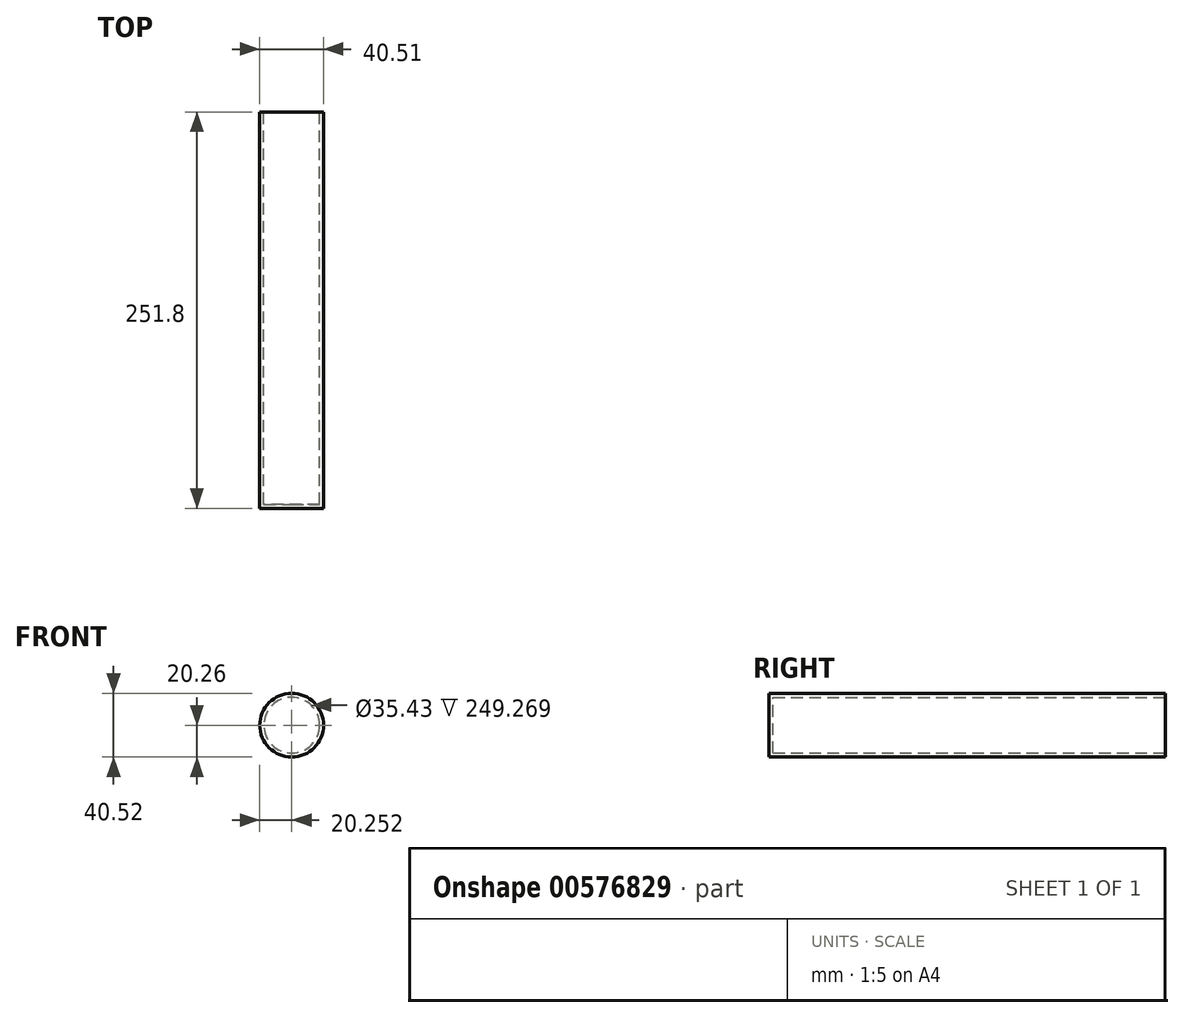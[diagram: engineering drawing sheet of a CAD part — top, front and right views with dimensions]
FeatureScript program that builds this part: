
annotation { "Feature Type Name" : "Feature", "Feature Type Description" : "" }
export const myFeature = defineFeature(function(context is Context, id is Id, definition is map)
    precondition{}
    {
        {
            var Q0;
            Q0=qCreatedBy(makeId("Top.planeOp"),FACE);
            var sketch = newSketch(context, id + "F0", { "sketchPlane" : qUnion([Q0])});
            skLineSegment(sketch, "E0.bottom", {"start": v(-59.71, 135.47) * mm, "end": v(-39.46, 135.47) * mm});
            skLineSegment(sketch, "E0.top", {"start": v(-59.71, -116.33) * mm, "end": v(-39.46, -116.33) * mm});
            skLineSegment(sketch, "E0.left", {"start": v(-59.71, 135.47) * mm, "end": v(-59.71, -116.33) * mm});
            skLineSegment(sketch, "E0.right", {"start": v(-39.46, 135.47) * mm, "end": v(-39.46, -116.33) * mm});
            skSolve(sketch);
        }
        {
            var Q0;
            Q0 = qSketchRegion(id + "F0", true);
            var Q1;
            Q1=sQuery(id+"F0.wireOp",EDGE,"E0.right");
            revolve(context, id + "F1", {"entities" : qUnion([Q0]), "axis" : qUnion([Q1]), "revolveType" : RevolveType.FULL});
        }
        {
            var Q0;
            Q0=makeQuery(id+"F1.opRevolve","SWEPT_FACE",FACE,{"disambiguationData":[OSD([sQuery(id+"F0.wireOp",EDGE,"E0.bottom")])]});
            shell(context, id + "F2", {"entities" : qUnion([Q0]), "thickness" : 2.54 * mm});
        }
    });
